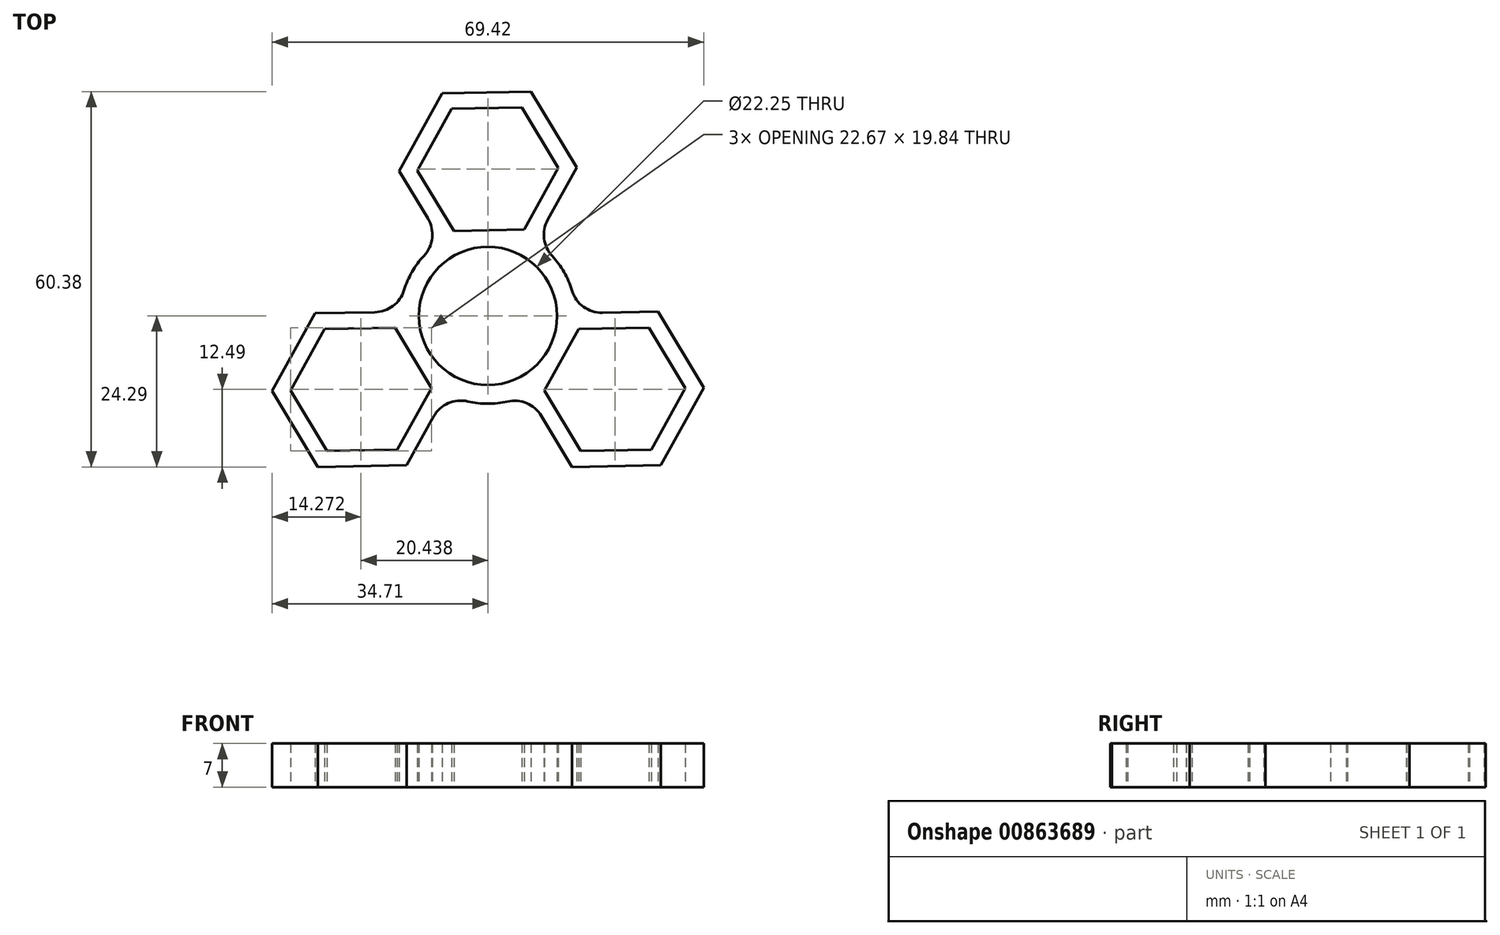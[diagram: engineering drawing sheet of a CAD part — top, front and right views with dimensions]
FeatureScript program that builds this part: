
annotation { "Feature Type Name" : "Feature", "Feature Type Description" : "" }
export const myFeature = defineFeature(function(context is Context, id is Id, definition is map)
    precondition{}
    {
        {
            var Q0;
            Q0=qCreatedBy(makeId("Top.planeOp"),FACE);
            var sketch = newSketch(context, id + "F0", { "sketchPlane" : qUnion([Q0])});
            skCircle(sketch, "E0", {"center": v(0, 0) * mm, "radius": 11.12 * mm});
            skLineSegment(sketch, "E1.0", {"start": v(-11.33, 23.4) * mm, "end": v(-5.85, 33.31) * mm});
            skLineSegment(sketch, "E1.1", {"start": v(-5.85, 33.31) * mm, "end": v(5.49, 33.52) * mm});
            skLineSegment(sketch, "E1.2", {"start": v(5.49, 33.52) * mm, "end": v(11.33, 23.8) * mm});
            skLineSegment(sketch, "E1.3", {"start": v(11.33, 23.8) * mm, "end": v(5.85, 13.89) * mm});
            skLineSegment(sketch, "E1.4", {"start": v(5.85, 13.89) * mm, "end": v(-5.49, 13.68) * mm});
            skLineSegment(sketch, "E1.5", {"start": v(-5.49, 13.68) * mm, "end": v(-11.33, 23.4) * mm});
            skPoint(sketch, "E1.0.midPoint", {"position": v(-8.6, 28.35) * mm});
            skLineSegment(sketch, "E2.0", {"start": v(-9.66, 15.67) * mm, "end": v(-14.27, 23.34) * mm});
            skLineSegment(sketch, "E2.1", {"start": v(-14.27, 23.34) * mm, "end": v(-7.36, 35.83) * mm});
            skLineSegment(sketch, "E2.2", {"start": v(-7.36, 35.83) * mm, "end": v(6.9, 36.09) * mm});
            skLineSegment(sketch, "E2.3", {"start": v(6.9, 36.09) * mm, "end": v(14.27, 23.86) * mm});
            skLineSegment(sketch, "E2.4", {"start": v(14.27, 23.86) * mm, "end": v(9.62, 15.45) * mm});
            skPoint(sketch, "E2.0.midPoint", {"position": v(-10.59, 17.22) * mm});
            skArc(sketch, "E3.0", {"start": v(-10.3, 9.67) * mm, "mid": v(-12.22, 7.09) * mm, "end": v(-13.5, 4.14) * mm});
            skLineSegment(sketch, "E4.1.0", {"start": v(-8.75, -16.2) * mm, "end": v(-13.08, -24.03) * mm});
            skLineSegment(sketch, "E4.1.1", {"start": v(-14.95, -1.88) * mm, "end": v(-9.1, -11.6) * mm});
            skLineSegment(sketch, "E4.1.2", {"start": v(-31.77, -12) * mm, "end": v(-26.29, -2.09) * mm});
            skLineSegment(sketch, "E4.1.3", {"start": v(-26.29, -2.09) * mm, "end": v(-14.95, -1.88) * mm});
            skLineSegment(sketch, "E4.1.4", {"start": v(-13.08, -24.03) * mm, "end": v(-27.35, -24.29) * mm});
            skPoint(sketch, "E4.1.5", {"position": v(-9.62, -17.78) * mm});
            skLineSegment(sketch, "E4.1.6", {"start": v(-34.7, -12.06) * mm, "end": v(-27.8, 0.43) * mm});
            skLineSegment(sketch, "E4.1.7", {"start": v(-14.6, -21.51) * mm, "end": v(-25.93, -21.72) * mm});
            skLineSegment(sketch, "E4.1.8", {"start": v(-25.93, -21.72) * mm, "end": v(-31.77, -12) * mm});
            skLineSegment(sketch, "E4.1.9", {"start": v(-27.35, -24.29) * mm, "end": v(-34.7, -12.06) * mm});
            skPoint(sketch, "E4.1.10", {"position": v(-20.26, -21.62) * mm});
            skLineSegment(sketch, "E4.1.11", {"start": v(-9.1, -11.6) * mm, "end": v(-14.6, -21.51) * mm});
            skLineSegment(sketch, "E4.1.12", {"start": v(-27.8, 0.43) * mm, "end": v(-18.2, 0.6) * mm});
            skLineSegment(sketch, "E4.2.0", {"start": v(18.4, 0.53) * mm, "end": v(27.35, 0.69) * mm});
            skLineSegment(sketch, "E4.2.1", {"start": v(9.1, -12) * mm, "end": v(14.6, -2.09) * mm});
            skLineSegment(sketch, "E4.2.2", {"start": v(26.29, -21.51) * mm, "end": v(14.95, -21.72) * mm});
            skLineSegment(sketch, "E4.2.3", {"start": v(14.95, -21.72) * mm, "end": v(9.1, -12) * mm});
            skLineSegment(sketch, "E4.2.4", {"start": v(27.35, 0.69) * mm, "end": v(34.7, -11.54) * mm});
            skPoint(sketch, "E4.2.5", {"position": v(20.21, 0.56) * mm});
            skLineSegment(sketch, "E4.2.6", {"start": v(27.8, -24.03) * mm, "end": v(13.53, -24.29) * mm});
            skLineSegment(sketch, "E4.2.7", {"start": v(25.93, -1.88) * mm, "end": v(31.77, -11.6) * mm});
            skLineSegment(sketch, "E4.2.8", {"start": v(31.77, -11.6) * mm, "end": v(26.29, -21.51) * mm});
            skLineSegment(sketch, "E4.2.9", {"start": v(34.7, -11.54) * mm, "end": v(27.8, -24.03) * mm});
            skPoint(sketch, "E4.2.10", {"position": v(28.85, -6.74) * mm});
            skLineSegment(sketch, "E4.2.11", {"start": v(14.6, -2.09) * mm, "end": v(25.93, -1.88) * mm});
            skLineSegment(sketch, "E4.2.12", {"start": v(13.53, -24.29) * mm, "end": v(8.57, -16.06) * mm});
            skArc(sketch, "E5.trimOffspring", {"start": v(-3.23, -13.75) * mm, "mid": v(-0.03, -14.12) * mm, "end": v(3.17, -13.76) * mm});
            skArc(sketch, "E6.trimOffspring", {"start": v(13.52, 4.08) * mm, "mid": v(12.25, 7.04) * mm, "end": v(10.34, 9.63) * mm});
            skPoint(sketch, "E7.newPointA", {"position": v(-6.9, 11.11) * mm});
            skArc(sketch, "E7.filletArc", {"start": v(-10.3, 9.67) * mm, "mid": v(-8.97, 12.57) * mm, "end": v(-9.66, 15.67) * mm});
            skPoint(sketch, "E8.newPointB", {"position": v(-13.53, 0.69) * mm});
            skArc(sketch, "E8.filletArc", {"start": v(-18.2, 0.6) * mm, "mid": v(-15.28, 1.61) * mm, "end": v(-13.5, 4.14) * mm});
            skPoint(sketch, "E9.newPointA", {"position": v(-6.17, -11.54) * mm});
            skArc(sketch, "E9.filletArc", {"start": v(-3.23, -13.75) * mm, "mid": v(-6.4, -14.05) * mm, "end": v(-8.75, -16.2) * mm});
            skPoint(sketch, "E10.newPointB", {"position": v(6.17, -12.06) * mm});
            skArc(sketch, "E10.filletArc", {"start": v(8.57, -16.06) * mm, "mid": v(6.24, -14.03) * mm, "end": v(3.17, -13.76) * mm});
            skPoint(sketch, "E11.newPointA", {"position": v(13.08, 0.43) * mm});
            skArc(sketch, "E11.filletArc", {"start": v(13.52, 4.08) * mm, "mid": v(15.37, 1.48) * mm, "end": v(18.4, 0.53) * mm});
            skPoint(sketch, "E12.newPointB", {"position": v(7.36, 11.37) * mm});
            skArc(sketch, "E12.filletArc", {"start": v(9.62, 15.45) * mm, "mid": v(9.03, 12.42) * mm, "end": v(10.34, 9.63) * mm});
            skSolve(sketch);
        }
        {
            var Q0;
            Q0 = qSketchRegion(id + "F0", true);
            extrude(context, id + "F1", {"entities" : qUnion([Q0]), "depth" : 7 * mm, "offsetDistance" : 25 * mm});
        }
    });
